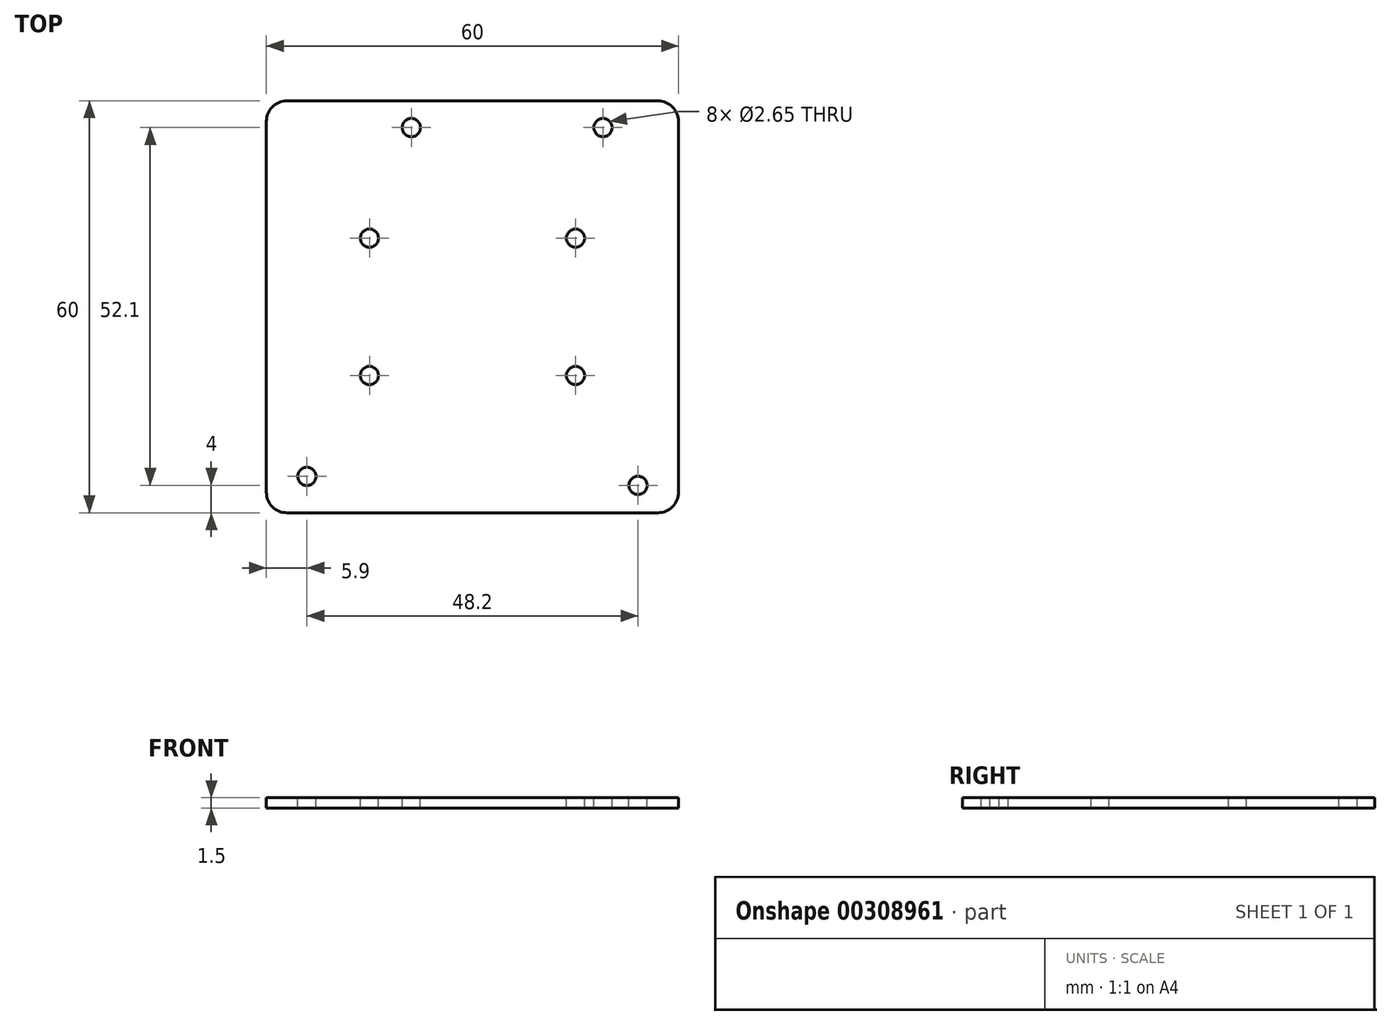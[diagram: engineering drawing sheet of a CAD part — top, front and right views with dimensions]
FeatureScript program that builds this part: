
annotation { "Feature Type Name" : "Feature", "Feature Type Description" : "" }
export const myFeature = defineFeature(function(context is Context, id is Id, definition is map)
    precondition{}
    {
        {
            var Q0;
            Q0=qCreatedBy(makeId("Top.planeOp"),FACE);
            var sketch = newSketch(context, id + "F0", { "sketchPlane" : qUnion([Q0])});
            skLineSegment(sketch, "E0.bottom", {"start": v(30, 30) * mm, "end": v(-30, 30) * mm});
            skLineSegment(sketch, "E0.top", {"start": v(30, -30) * mm, "end": v(-30, -30) * mm});
            skLineSegment(sketch, "E0.left", {"start": v(30, 30) * mm, "end": v(30, -30) * mm});
            skLineSegment(sketch, "E0.right", {"start": v(-30, 30) * mm, "end": v(-30, -30) * mm});
            skPoint(sketch, "E0.middle", {"position": v(0, 0) * mm});
            skSolve(sketch);
        }
        {
            var Q0;
            Q0=makeQuery(id+"F0.imprint","IMPRINT",FACE,{"disambiguationData":[TD([[makeQuery(id+"F0.imprint","IMPRINT",EDGE,{"derivedFrom":sQuery(id+"F0.wireOp",EDGE,"E0.bottom")}),1.0]])]});
            extrude(context, id + "F1", {"entities" : qUnion([Q0]), "depth" : 1.5 * mm, "offsetDistance" : 25 * mm});
        }
        {
            var Q0;
            Q0=makeQuery(id+"F1.opExtrude","SWEPT_EDGE",EDGE,{"disambiguationData":[OSD([sQuery(id+"F0.wireOp",EDGE,"E0.top"),sQuery(id+"F0.wireOp",EDGE,"E0.right")])]});
            var Q1;
            Q1=makeQuery(id+"F1.opExtrude","SWEPT_EDGE",EDGE,{"disambiguationData":[OSD([sQuery(id+"F0.wireOp",EDGE,"E0.top"),sQuery(id+"F0.wireOp",EDGE,"E0.left")])]});
            var Q2;
            Q2=makeQuery(id+"F1.opExtrude","SWEPT_EDGE",EDGE,{"disambiguationData":[OSD([sQuery(id+"F0.wireOp",EDGE,"E0.bottom"),sQuery(id+"F0.wireOp",EDGE,"E0.left")])]});
            var Q3;
            Q3=makeQuery(id+"F1.opExtrude","SWEPT_EDGE",EDGE,{"disambiguationData":[OSD([sQuery(id+"F0.wireOp",EDGE,"E0.bottom"),sQuery(id+"F0.wireOp",EDGE,"E0.right")])]});
            fillet(context, id + "F2", {"entities" : qUnion([Q0, Q1, Q2, Q3]), "radius" : 3 * mm, "tangentPropagation" : true, "allowEdgeOverflow" : false});
        }
        {
            var Q0;
            Q0=makeQuery(id+"F1.opExtrude","CAP_FACE",FACE,{"disambiguationData":[OSD([sQuery(id+"F0.wireOp",EDGE,"E0.bottom"),sQuery(id+"F0.wireOp",EDGE,"E0.top"),sQuery(id+"F0.wireOp",EDGE,"E0.left"),sQuery(id+"F0.wireOp",EDGE,"E0.right")])],"isStart":false});
            var sketch = newSketch(context, id + "F3", { "sketchPlane" : qUnion([Q0])});
            skLineSegment(sketch, "E1.bottom", {"start": v(15, 10) * mm, "end": v(-15, 10) * mm});
            skLineSegment(sketch, "E1.top", {"start": v(15, -10) * mm, "end": v(-15, -10) * mm});
            skLineSegment(sketch, "E1.left", {"start": v(15, 10) * mm, "end": v(15, -10) * mm});
            skLineSegment(sketch, "E1.right", {"start": v(-15, 10) * mm, "end": v(-15, -10) * mm});
            skPoint(sketch, "E1.middle", {"position": v(0, 0) * mm});
            skLineSegment(sketch, "E2", {"start": v(-8.9, 26.1) * mm, "end": v(19, 26.1) * mm});
            skLineSegment(sketch, "E3", {"start": v(19, 26.1) * mm, "end": v(24.1, -26) * mm});
            skLineSegment(sketch, "E4", {"start": v(24.1, -26) * mm, "end": v(-24.1, -24.7) * mm});
            skLineSegment(sketch, "E5", {"start": v(-24.1, -24.7) * mm, "end": v(-8.9, 26.1) * mm});
            skLineSegment(sketch, "E6", {"start": v(24.1, -26) * mm, "end": v(30, -26) * mm});
            skLineSegment(sketch, "E7", {"start": v(-24.1, -24.7) * mm, "end": v(-30, -24.7) * mm});
            skSolve(sketch);
        }
        {
            var Q0;
            Q0=sQuery(id+"F3.wireOp",VERTEX,"E1.bottom.end");
            var Q1;
            Q1=sQuery(id+"F3.wireOp",VERTEX,"E1.bottom.start");
            var Q2;
            Q2=sQuery(id+"F3.wireOp",VERTEX,"E1.top.start");
            var Q3;
            Q3=sQuery(id+"F3.wireOp",VERTEX,"E1.top.end");
            var Q4;
            Q4=sQuery(id+"F3.wireOp",VERTEX,"E2.start");
            var Q5;
            Q5=sQuery(id+"F3.wireOp",VERTEX,"E2.end");
            var Q6;
            Q6=sQuery(id+"F3.wireOp",VERTEX,"E3.end");
            var Q7;
            Q7=sQuery(id+"F3.wireOp",VERTEX,"E4.end");
            var Q8;
            Q8=makeQuery(id+"F1.opExtrude","SWEPT_BODY",BODY,{"disambiguationData":[OSD([sQuery(id+"F0.wireOp",EDGE,"E0.bottom"),sQuery(id+"F0.wireOp",EDGE,"E0.top"),sQuery(id+"F0.wireOp",EDGE,"E0.left"),sQuery(id+"F0.wireOp",EDGE,"E0.right")])]});
            hole(context, id + "F4", {"style" : HoleStyle.SIMPLE, "endStyle" : HoleEndStyle.THROUGH, "standardTappedOrClearance" : lookupTablePath({ "standard" : "ISO", "engagement" : "75%", "pitch" : "0.35 mm", "size" : "M3", "type" : "Tapped" }), "standardBlindInLast" : lookupTablePath({ "standard" : "ISO", "fit" : "Normal", "engagement" : "75%", "pitch" : "0.35 mm", "size" : "M3", "type" : "Clearance & tapped" }), "holeDiameter" : 2.65 * mm, "majorDiameter" : 3 * mm, "showTappedDepth" : true, "tappedDepth" : 12 * mm, "tapClearance" : 3, "locations" : qUnion([Q0, Q1, Q2, Q3, Q4, Q5, Q6, Q7]), "scope" : qUnion([Q8])});
        }
    });
